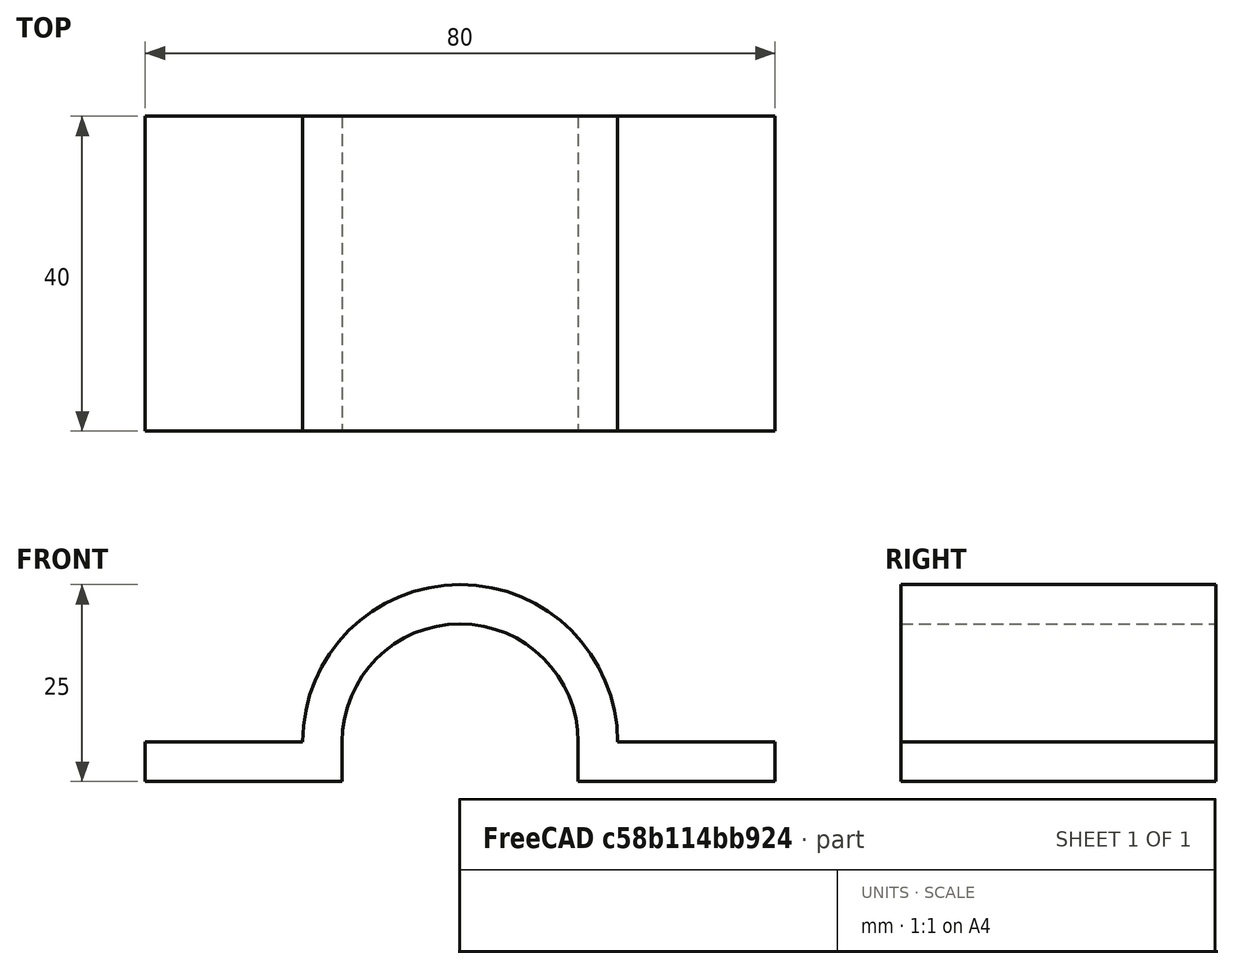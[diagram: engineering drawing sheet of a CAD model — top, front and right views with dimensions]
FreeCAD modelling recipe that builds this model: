
FCSTD DOCUMENT  (FreeCAD 0.21R33771 (Git))
Label: OJT1_T21P01_brida
License: All rights reserved
LicenseURL: https://en.wikipedia.org/wiki/All_rights_reserved
objects: Sketcher::SketchObject×2, PartDesign::Pad×1, PartDesign::Body×1
note: 5 computed .brp shape members not serialized (recipe doc carries the construction recipe); baked Part::Feature solids carry a one-line shape summary decoded from their .brp

FEATURE [Sketcher::SketchObject] Sketch  label="brida"
  FullyConstrained = true
  MapMode = 5
  Placement = pos=(0,0,0) rot=(1,0,0;1.5708rad)
  Support = -> [XZ_Plane]
  sketch-geometry (11):
    g0: ArcOfCircle CenterX=0 CenterY=0 CenterZ=0 NormalX=0 NormalY=0 NormalZ=1 AngleXU=0 Radius=20 StartAngle=-1.15e-14 EndAngle=3.14159
    g1: LineSegment StartX=20 StartY=-2.309e-13 StartZ=0 EndX=40 EndY=-2.309e-13 EndZ=0
    g2: ArcOfCircle CenterX=0 CenterY=0 CenterZ=0 NormalX=0 NormalY=0 NormalZ=1 AngleXU=0 Radius=15 StartAngle=-6.2e-15 EndAngle=3.14159
    g3: LineSegment StartX=-15 StartY=-1.381e-13 StartZ=0 EndX=-15 EndY=-5 EndZ=0
    g4: LineSegment StartX=15 StartY=-9.33e-14 StartZ=0 EndX=15 EndY=-5 EndZ=0
    g5: LineSegment StartX=-15 StartY=-5 StartZ=0 EndX=-40 EndY=-5 EndZ=0
    g6: LineSegment StartX=-40 StartY=-5 StartZ=0 EndX=-40 EndY=-3.171e-13 EndZ=0
    g7: LineSegment StartX=15 StartY=-5 StartZ=0 EndX=40 EndY=-5 EndZ=0
    g8: LineSegment StartX=40 StartY=-5 StartZ=0 EndX=40 EndY=-2.309e-13 EndZ=0
    g9: LineSegment StartX=-40 StartY=-3.171e-13 StartZ=0 EndX=-20 EndY=-3.171e-13 EndZ=0
    g10: LineSegment StartX=-20 StartY=-3.171e-13 StartZ=0 EndX=-15 EndY=-1.381e-13 EndZ=0
  constraints (30):
    c: Horizontal(g1)
    c: Coincident(g0,g1)
    c: Perpendicular(g0,g1)
    c: Coincident(g0,g2)
    c: Vertical(g3)
    c: Vertical(g4)
    c: Tangent(g2,g3) = -1.5708
    c: Tangent(g2,g4) = 1.5708
    c: Equal(g4,g3)
    c: Coincident(g5,g6)
    c: Coincident(g7,g8)
    c: Coincident(g3,g5)
    c: Coincident(g4,g7)
    c: Horizontal(g7)
    c: Horizontal(g5)
    c: Equal(g7,g5)
    c: Vertical(g6)
    c: Vertical(g8)
    c: Coincident(g1,g8)
    c: Horizontal(g9)
    c: Coincident(g0,g9)
    c: Coincident(g6,g9)
    c: Coincident(g0,g-1)
    c: Perpendicular(g0,g9)
    c: Coincident(g2,g10)
    c: Equal(g3,g10)
    c: Coincident(g0,g10)
    c: DistanceX(g0,g2) = 5
    c: Radius(g2) = 15
    c: DistanceX(g6,g9) = 20
FEATURE [PartDesign::Pad] Pad
  Direction = (0,-1,2e-16)
  Length = 40
  Length2 = 10
  Midplane = true
  Placement = pos=(0,0,0) rot=(1,0,0;1.5708rad)
  Profile = -> Sketch
  ReferenceAxis = -> Sketch [N_Axis]
  Type = 0
FEATURE [Sketcher::SketchObject] Sketch001  label="forats"
  FullyConstrained = false
  MapMode = 5
  Placement = pos=(0,0,-3.171e-13) rot=(0,0,1;3.14159rad)
  Support = -> [Pad]
  sketch-geometry (5):
    g0: Circle CenterX=-30 CenterY=0 CenterZ=0 NormalX=0 NormalY=0 NormalZ=1 AngleXU=0 Radius=4
    g1: Circle CenterX=30 CenterY=0 CenterZ=0 NormalX=0 NormalY=0 NormalZ=1 AngleXU=0 Radius=4
    g2: LineSegment StartX=-40 StartY=-51 StartZ=0 EndX=-40 EndY=-20 EndZ=0
    g3: LineSegment StartX=-20 StartY=-18 StartZ=0 EndX=-20 EndY=-34.6611 EndZ=0
    g4: LineSegment StartX=40 StartY=-20 StartZ=0 EndX=40 EndY=-30 EndZ=0
  constraints (12):
    c: Radius(g0) = 4
    c: Equal(g1,g0)
    c: Vertical(g2)
    c: Vertical(g3)
    c: DistanceX(g0,g3) = 10
    c: Vertical(g4)
    c: DistanceX(g1,g4) = 10
    c: DistanceX(g0,g1) = 60
    c: DistanceY(g4,g1) = 20
    c: Symmetric(g1,g0,g-2)
    c: Symmetric(g4,g2,g-2)
    c: DistanceY(g1) = 0
FEATURE [PartDesign::Body] Body
  Group = -> [Sketch,Pad,Sketch001]
  Origin = -> Origin
  Tip = -> Pad
